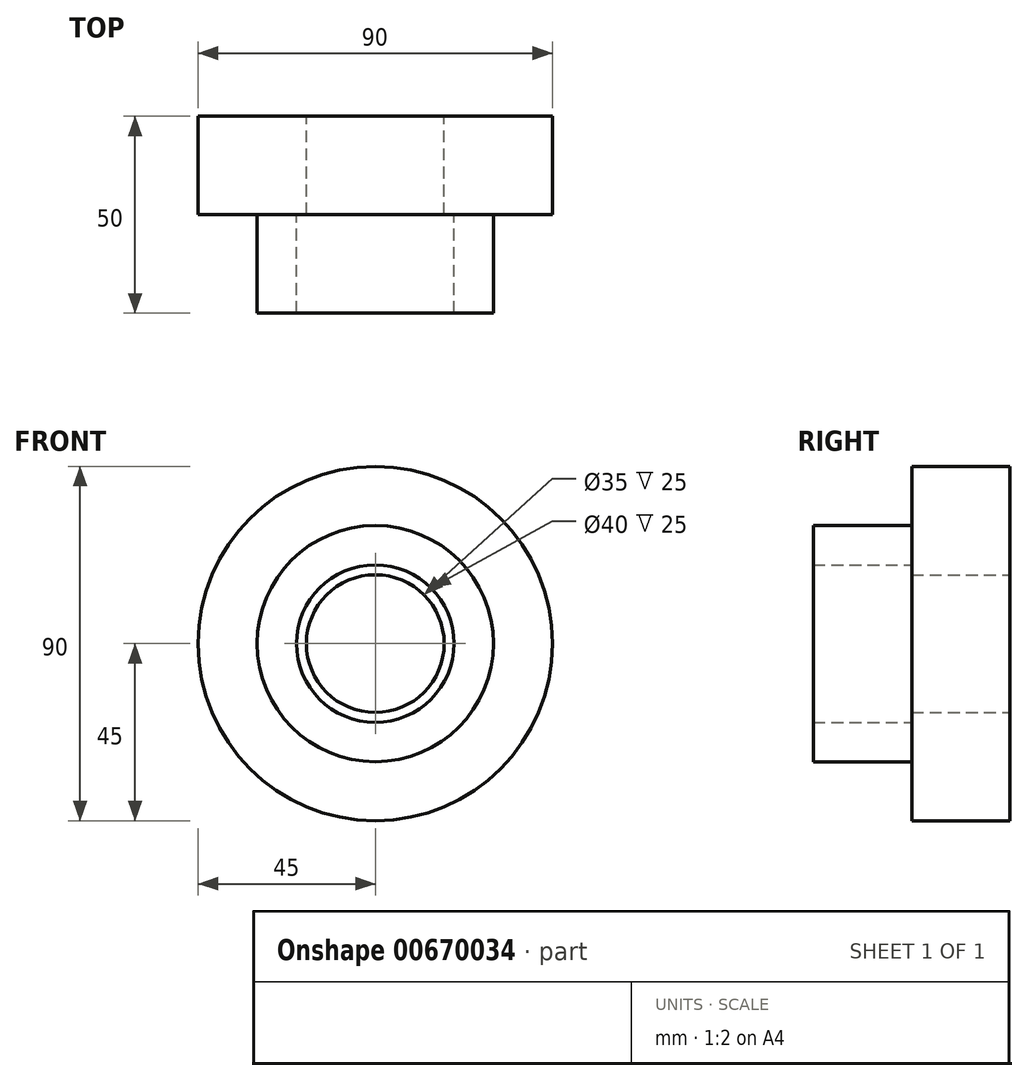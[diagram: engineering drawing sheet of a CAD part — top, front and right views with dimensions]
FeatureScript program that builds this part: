
annotation { "Feature Type Name" : "Feature", "Feature Type Description" : "" }
export const myFeature = defineFeature(function(context is Context, id is Id, definition is map)
    precondition{}
    {
        {
            var Q0;
            Q0=qCreatedBy(makeId("Front.planeOp"),FACE);
            var sketch = newSketch(context, id + "F0", { "sketchPlane" : qUnion([Q0])});
            skCircle(sketch, "E0", {"center": v(0, 0) * mm, "radius": 17.5 * mm});
            skCircle(sketch, "E1", {"center": v(0, 0) * mm, "radius": 45 * mm});
            skSolve(sketch);
        }
        {
            var Q0;
            Q0=makeQuery(id+"F0.imprint","IMPRINT",FACE,{"disambiguationData":[TD([[makeQuery(id+"F0.imprint","IMPRINT",EDGE,{"derivedFrom":sQuery(id+"F0.wireOp",EDGE,"E0")}),-1.0]])]});
            extrude(context, id + "F1", {"entities" : qUnion([Q0]), "depth" : 25 * mm, "offsetDistance" : 25 * mm});
        }
        {
            var Q0;
            Q0=makeQuery(id+"F1.opExtrude","CAP_FACE",FACE,{"disambiguationData":[OSD([sQuery(id+"F0.wireOp",EDGE,"E0"),sQuery(id+"F0.wireOp",EDGE,"E1")])],"isStart":false});
            var sketch = newSketch(context, id + "F2", { "sketchPlane" : qUnion([Q0])});
            skCircle(sketch, "E2", {"center": v(0, 0) * mm, "radius": 20 * mm});
            skCircle(sketch, "E3", {"center": v(0, 0) * mm, "radius": 30 * mm});
            skSolve(sketch);
        }
        {
            var Q0;
            Q0=makeQuery(id+"F2.imprint","IMPRINT",FACE,{"disambiguationData":[TD([[makeQuery(id+"F2.imprint","IMPRINT",EDGE,{"derivedFrom":sQuery(id+"F2.wireOp",EDGE,"E2")}),-1.0]])]});
            extrude(context, id + "F3", {"entities" : qUnion([Q0]), "operationType" : NewBodyOperationType.ADD, "depth" : 25 * mm, "offsetDistance" : 25 * mm});
        }
    });
